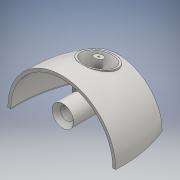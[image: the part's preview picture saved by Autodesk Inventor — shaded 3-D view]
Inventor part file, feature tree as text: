
AUTODESK INVENTOR PART (.ipt)
format: ipt  version: 2016 (Build 200138000, 138)  size: 365,568 bytes
history: native  units: mm
features: sketch x15, extrude x8, plane x6, other x4, loft x3, shell x1, hole x1, chamfer x1
ambient origin geometry x8: Origin, YZ Plane, XZ Plane, XY Plane, X Axis, Y Axis, Z Axis, Center Point
bodies: Solid1 (feature_tree)
feature tree (39):
  sketch  "Sketch1"  dims[d0=32.5mm d1=17.0mm]
  plane  "Work Plane1"
  sketch  "Sketch2"  dims[d2=26.5mm d3=4.0mm d4=32.5mm]
  plane  "Work Plane2"
  loft  "Loft1"
  extrude  "Extrusion1"  Depth=4.0mm
  plane  "Work Plane3"
  sketch  "Sketch5"  dims[d14=10.0mm d15=11.0mm]
  shell  "Shell1"  Thickness=32.5mm
  extrude  "Extrusion2"  TaperAngle=0.0deg  [1 undecoded]
  hole  "Hole1"  [1 undecoded]
  chamfer  "Chamfer1"  Distance=10.0mm
  extrude  "Extrusion3"  Depth=10.0mm
  plane  "Work Plane4"
  extrude  "Extrusion4"  Depth=6.5mm
  plane  "Work Plane5"
  sketch  "Sketch10"  dims[d31=5.0mm d32=0.0mm d33=5.6mm]
  other  "Work Point1"
  extrude  "Extrusion5"  Depth=15.8mm TaperAngle=0.0deg
  extrude  "Extrusion6"  Depth=1.3mm TaperAngle=45.0deg
  loft  "Loft2"
  sketch  "Sketch13"  dims[d39=3.5mm d40=0.0mm d41=3.5mm d42=0.0mm]
  plane  "Work Plane6"
  loft  "Loft3"
  extrude  "Extrusion7"  Depth=10.0mm
  extrude  "Extrusion8"  Depth=3.5mm TaperAngle=0.0deg
  sketch  "Sketch3"  dims[d5=0.0mm d6=90.0deg d7=0.0mm d8=90.0deg]
  sketch  "Sketch4"  dims[d9=0.0mm d10=90.0deg d11=16.5mm d12=10.0mm d13=0.0mm]
  sketch  "Sketch6"  dims[d16=0.9mm d17=6.5mm]
  sketch  "Sketch7"  dims[d18=5.75mm d19=15.8mm d20=0.0mm]
  sketch  "Sketch8"  dims[d21=3.9mm d22=6.0mm d23=4.0mm d24=2.0mm d25=90.0deg d26=5.0mm d27=20.594885mm d28=1.3mm d29=2.0mm d30=45.0deg]
  other  "Work Axis1"
  sketch  "Sketch11"  dims[d34=10.0mm d35=1.5mm d36=0.0mm]
  sketch  "Sketch12"  dims[d37=3.75mm d38=10.0mm]
  other  "Edges1"
  other  "Edges2"
  sketch  "Sketch14"  dims[d43=0.0mm d44=90.0deg]
  sketch  "Sketch15"  dims[d45=0.0mm d46=90.0deg]
  sketch  "Sketch16"  dims[d47=9.0mm d48=-5.0mm d49=4.0mm d51=0.0mm d52=90.0deg d53=0.0mm d54=90.0deg d55=2.6mm d56=5.7mm d57=0.0mm d58=0.6mm d59=5.7mm d60=0.0mm]
note: 2 required parameter values undecoded (feature->parameter linkage not recoverable at this tier; creation-order binding heuristic only, values carry confidence <= 0.55)
